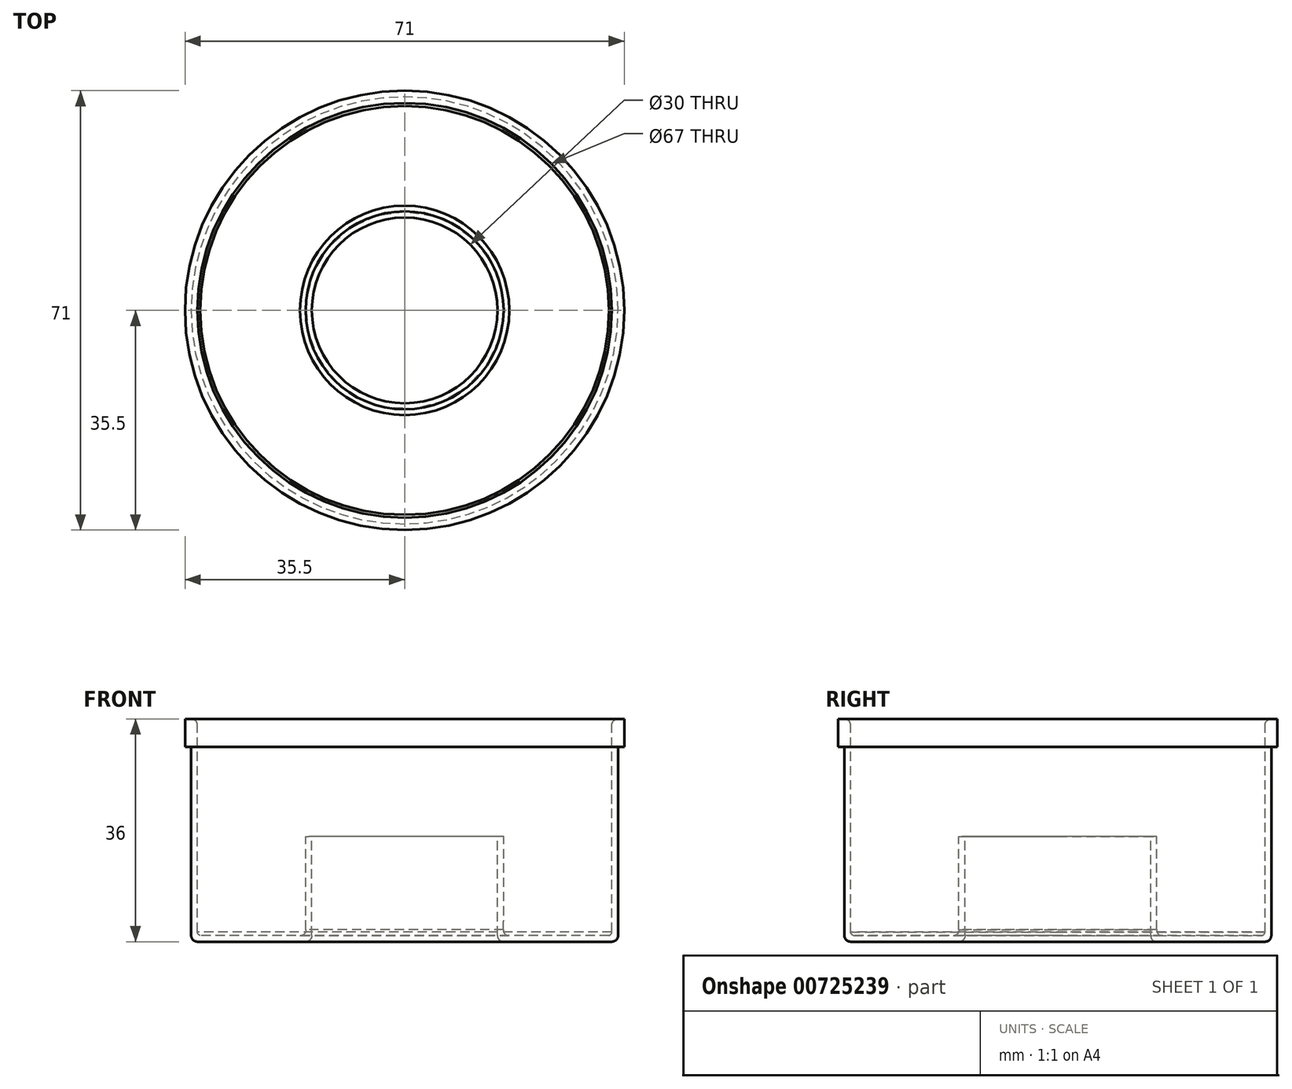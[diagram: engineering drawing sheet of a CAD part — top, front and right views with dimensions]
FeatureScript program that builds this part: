
annotation { "Feature Type Name" : "Feature", "Feature Type Description" : "" }
export const myFeature = defineFeature(function(context is Context, id is Id, definition is map)
    precondition{}
    {
        {
            var Q0;
            Q0=qCreatedBy(makeId("Front.planeOp"),FACE);
            var sketch = newSketch(context, id + "F0", { "sketchPlane" : qUnion([Q0])});
            skLineSegment(sketch, "E0", {"start": v(0, 0) * mm, "end": v(-33.5, 0) * mm});
            skLineSegment(sketch, "E1", {"start": v(-34.5, 1) * mm, "end": v(-34.5, 31.5) * mm});
            skLineSegment(sketch, "E2", {"start": v(-34.5, 31.5) * mm, "end": v(-35.5, 31.5) * mm});
            skLineSegment(sketch, "E3", {"start": v(-35.5, 31.5) * mm, "end": v(-35.5, 36) * mm});
            skLineSegment(sketch, "E4", {"start": v(-35.5, 36) * mm, "end": v(-33.5, 36) * mm});
            skLineSegment(sketch, "E5", {"start": v(-33.5, 36) * mm, "end": v(-33.5, 1.59) * mm});
            skLineSegment(sketch, "E6", {"start": v(-33.5, 1) * mm, "end": v(-33.49, 1) * mm});
            skLineSegment(sketch, "E7", {"start": v(-16, 1) * mm, "end": v(-16, 1.03) * mm});
            skLineSegment(sketch, "E8", {"start": v(-15, 17) * mm, "end": v(-15, 1) * mm});
            skLineSegment(sketch, "E9", {"start": v(-15, 1) * mm, "end": v(-15, 1) * mm});
            skLineSegment(sketch, "E10", {"start": v(0, 31.14) * mm, "end": v(0, -10.74) * mm, "construction": true});
            skArc(sketch, "E11", {"start": v(-34.5, 1) * mm, "mid": v(-34.2, 0.3) * mm, "end": v(-33.5, 0) * mm});
            skLineSegment(sketch, "E12", {"start": v(-34.5, 0) * mm, "end": v(-29.65, 4.8) * mm, "construction": true});
            skArc(sketch, "E13", {"start": v(-33.5, 1.59) * mm, "mid": v(-33.31, 1.16) * mm, "end": v(-32.88, 0.98) * mm});
            skLineSegment(sketch, "E14.trimOffspring", {"start": v(-33.03, 1) * mm, "end": v(-16.14, 1) * mm});
            skLineSegment(sketch, "E15", {"start": v(-33.5, 0) * mm, "end": v(-15, 0) * mm});
            skLineSegment(sketch, "E16", {"start": v(-33.5, 0) * mm, "end": v(0, 0) * mm});
            skLineSegment(sketch, "E17", {"start": v(-15, 0) * mm, "end": v(-21.65, 6.83) * mm, "construction": true});
            skArc(sketch, "E18", {"start": v(-15, 1) * mm, "mid": v(-15.3, 0.3) * mm, "end": v(-16, 0) * mm});
            skLineSegment(sketch, "E19.trimOffspring", {"start": v(-16, 4.26) * mm, "end": v(-16, 17) * mm});
            skArc(sketch, "E20", {"start": v(-15, 17) * mm, "mid": v(-15.5, 17.01) * mm, "end": v(-16, 17) * mm});
            skLineSegment(sketch, "E21", {"start": v(-26.04, 1) * mm, "end": v(-26.04, 42) * mm, "construction": true});
            skLineSegment(sketch, "E22", {"start": v(-23, 42) * mm, "end": v(-23, 9) * mm, "construction": true});
            skArc(sketch, "E23", {"start": v(-16.9, 1) * mm, "mid": v(-16.21, 1.25) * mm, "end": v(-15.99, 1.95) * mm});
            skLineSegment(sketch, "E24", {"start": v(-15.99, 1.95) * mm, "end": v(-16, 4.26) * mm});
            skLineSegment(sketch, "E25", {"start": v(0, 10.2) * mm, "end": v(-23, 10.2) * mm, "construction": true});
            skSolve(sketch);
        }
        {
            var Q0;
            {var subQ0=sQuery(id+"F0.wireOp",EDGE,"E1");Q0=makeQuery(id+"F0.imprint","IMPRINT",FACE,{"disambiguationData":[TD([[makeQuery(id+"F0.imprint","IMPRINT",EDGE,{"derivedFrom":subQ0}),-1.0]])]});}
            var Q1;
            Q1=sQuery(id+"F0.wireOp",EDGE,"E10");
            revolve(context, id + "F1", {"surfaceOperationType" : NewSurfaceOperationType.NEW, "entities" : qUnion([Q0]), "axis" : qUnion([Q1]), "revolveType" : RevolveType.FULL});
        }
        {
            var Q0;
            Q0=makeQuery(id+"F1.opRevolve","SWEPT_EDGE",EDGE,{"disambiguationData":[OSD([sQuery(id+"F0.wireOp",EDGE,"E4"),sQuery(id+"F0.wireOp",EDGE,"E5")])]});
            fillet(context, id + "F2", {"entities" : qUnion([Q0]), "tangentPropagation" : true, "radius" : 1 * mm, "defaultsChanged" : false, "vertexSettings" : [], "allowEdgeOverflow" : false});
        }
    });
